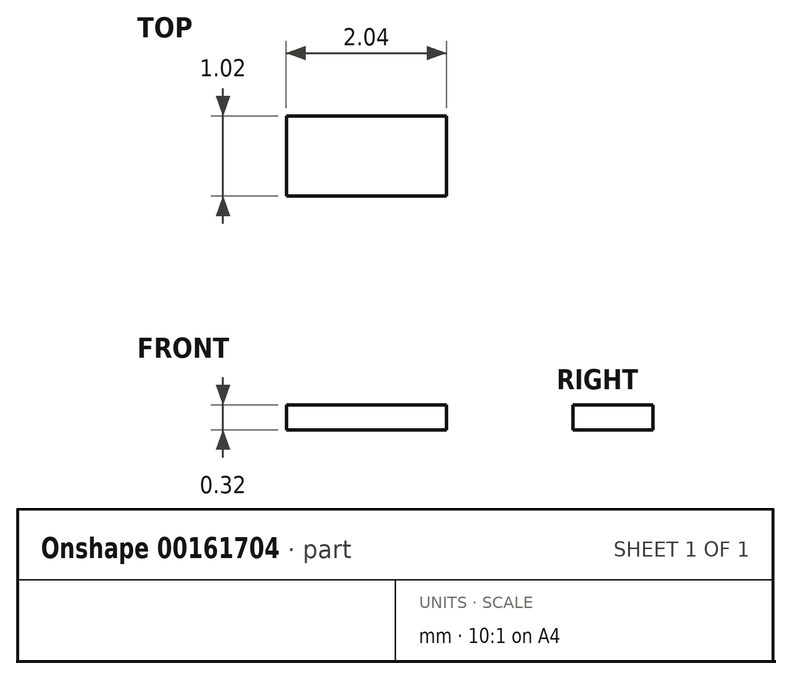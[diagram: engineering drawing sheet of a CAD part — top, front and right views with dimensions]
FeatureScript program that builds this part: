
annotation { "Feature Type Name" : "Feature", "Feature Type Description" : "" }
export const myFeature = defineFeature(function(context is Context, id is Id, definition is map)
    precondition{}
    {
        {
            var Q0;
            Q0=qCreatedBy(makeId("Top.planeOp"),FACE);
            var sketch = newSketch(context, id + "F0", { "sketchPlane" : qUnion([Q0])});
            skLineSegment(sketch, "E0.bottom", {"start": v(1.02, 0.5) * mm, "end": v(-1.02, 0.5) * mm});
            skLineSegment(sketch, "E0.top", {"start": v(1.02, -0.5) * mm, "end": v(-1.02, -0.5) * mm});
            skLineSegment(sketch, "E0.left", {"start": v(1.02, 0.5) * mm, "end": v(1.02, -0.5) * mm});
            skLineSegment(sketch, "E0.right", {"start": v(-1.02, 0.5) * mm, "end": v(-1.02, -0.5) * mm});
            skPoint(sketch, "E0.middle", {"position": v(0, 0) * mm});
            skSolve(sketch);
        }
        {
            var Q0;
            Q0=makeQuery(id+"F0.imprint","IMPRINT",FACE,{"disambiguationData":[TD([[makeQuery(id+"F0.imprint","IMPRINT",EDGE,{"derivedFrom":sQuery(id+"F0.wireOp",EDGE,"E0.bottom")}),1.0]])]});
            extrude(context, id + "F1", {"entities" : qUnion([Q0]), "depth" : 0.32 * mm});
        }
    });
